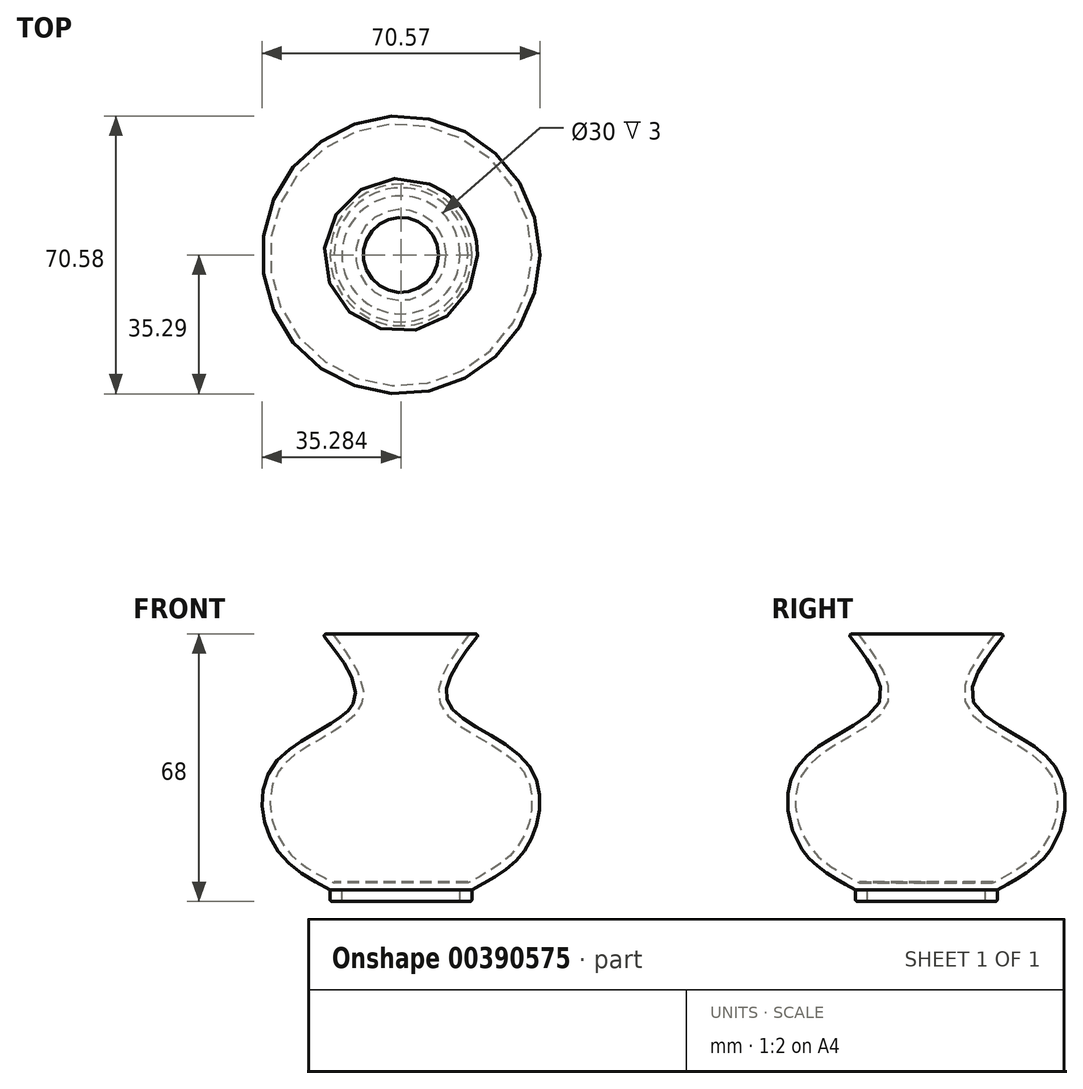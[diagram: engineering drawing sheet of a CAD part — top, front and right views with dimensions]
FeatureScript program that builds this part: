
annotation { "Feature Type Name" : "Feature", "Feature Type Description" : "" }
export const myFeature = defineFeature(function(context is Context, id is Id, definition is map)
    precondition{}
    {
        {
            var Q0;
            Q0=qCreatedBy(makeId("Front.planeOp"),FACE);
            var sketch = newSketch(context, id + "F0", { "sketchPlane" : qUnion([Q0])});
            skLineSegment(sketch, "E0", {"start": v(19.43, 45.87) * mm, "end": v(19.43, -19.13) * mm});
            skLineSegment(sketch, "E1", {"start": v(19.43, -19.13) * mm, "end": v(34.43, -19.13) * mm});
            skLineSegment(sketch, "E2", {"start": v(34.43, -19.13) * mm, "end": v(34.43, -22.13) * mm});
            skLineSegment(sketch, "E3", {"start": v(34.43, -22.13) * mm, "end": v(37.43, -22.13) * mm});
            skLineSegment(sketch, "E4", {"start": v(19.43, 45.87) * mm, "end": v(39.43, 45.87) * mm});
            skLineSegment(sketch, "E5", {"start": v(37.43, -22.13) * mm, "end": v(37.43, -19.13) * mm});
            skFitSpline(sketch, "E6", {"points": [v(39.43, 45.87) * mm, v(31.54, 28.25) * mm, v(51.6, 12.91) * mm, v(51.6, -8.03) * mm, v(37.43, -19.13) * mm], "startDerivative": vector(-63.4, -80.13) * mm, "endDerivative": vector(-69.9, -36.38) * mm});
            skSolve(sketch);
        }
        {
            var Q0;
            Q0 = qSketchRegion(id + "F0", true);
            var Q1;
            Q1=sQuery(id+"F0.wireOp",EDGE,"E0");
            revolve(context, id + "F1", {"entities" : qUnion([Q0]), "axis" : qUnion([Q1]), "revolveType" : RevolveType.FULL});
        }
        {
            var Q0;
            Q0=makeQuery(id+"F1.opRevolve","SWEPT_FACE",FACE,{"disambiguationData":[OSD([sQuery(id+"F0.wireOp",EDGE,"E4")])]});
            shell(context, id + "F2", {"entities" : qUnion([Q0]), "thickness" : 2 * mm});
        }
        {
            var Q0;
            Q0=makeQuery(id+"F1.opRevolve","SWEPT_EDGE",EDGE,{"disambiguationData":[OSD([sQuery(id+"F0.wireOp",EDGE,"E3"),sQuery(id+"F0.wireOp",EDGE,"E5")])]});
            var Q1;
            Q1=makeQuery(id+"F1.opRevolve","SWEPT_EDGE",EDGE,{"disambiguationData":[OSD([sQuery(id+"F0.wireOp",EDGE,"E4"),sQuery(id+"F0.wireOp",EDGE,"E6")])]});
            var Q2;
            Q2=makeQuery(id+"F2.opShell","OFFSET_EDGE",EDGE,{"disambiguationData":[OSD([sQuery(id+"F0.wireOp",EDGE,"E4"),sQuery(id+"F0.wireOp",EDGE,"E6")])]});
            fillet(context, id + "F3", {"entities" : qUnion([Q0, Q1, Q2]), "radius" : 0.5 * mm, "tangentPropagation" : true, "allowEdgeOverflow" : false});
        }
    });
